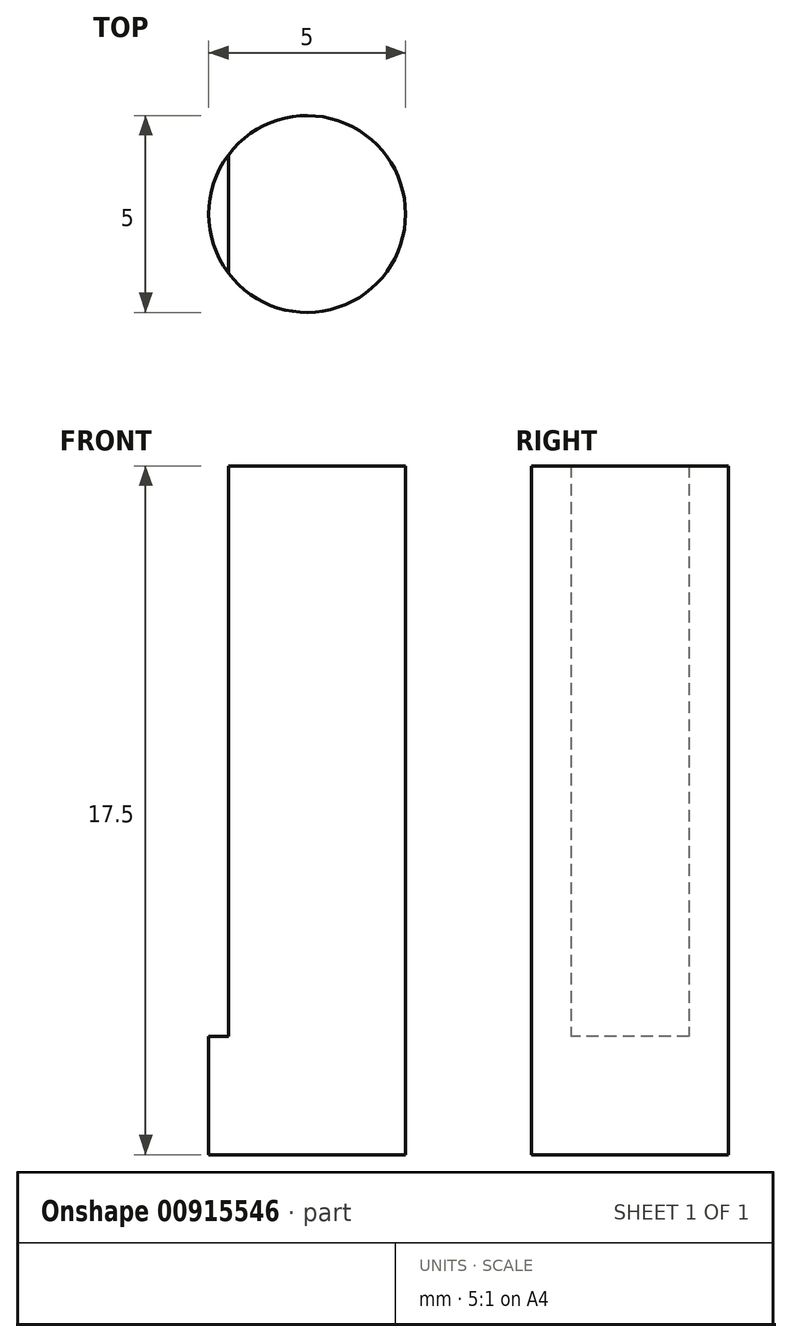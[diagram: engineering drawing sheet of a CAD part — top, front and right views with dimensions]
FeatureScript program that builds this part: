
annotation { "Feature Type Name" : "Feature", "Feature Type Description" : "" }
export const myFeature = defineFeature(function(context is Context, id is Id, definition is map)
    precondition{}
    {
        {
            var Q0;
            Q0=qCreatedBy(makeId("Top.planeOp"),FACE);
            var sketch = newSketch(context, id + "F0", { "sketchPlane" : qUnion([Q0])});
            skCircle(sketch, "E0.0", {"center": v(0, 0) * mm, "radius": 11 * mm});
            skCircle(sketch, "E1.0", {"center": v(0, 0) * mm, "radius": 16.5 * mm});
            skCircle(sketch, "E2.0", {"center": v(0, 0) * mm, "radius": 2.5 * mm});
            skLineSegment(sketch, "E3.0", {"start": v(-2, 1.5) * mm, "end": v(-2, -1.5) * mm});
            skSolve(sketch);
        }
        {
            var Q0;
            {var subQ0=sQuery(id+"F0.wireOp",EDGE,"E3.0");Q0=makeQuery(id+"F0.imprint","IMPRINT",FACE,{"disambiguationData":[TD([[makeQuery(id+"F0.imprint","IMPRINT",EDGE,{"derivedFrom":subQ0}),1.0]])]});}
            extrude(context, id + "F1", {"entities" : qUnion([Q0]), "depth" : 17.5 * mm, "offsetDistance" : 25 * mm});
        }
        {
            var Q0;
            {var subQ0=sQuery(id+"F0.wireOp",EDGE,"E3.0");Q0=makeQuery(id+"F0.imprint","IMPRINT",FACE,{"disambiguationData":[TD([[makeQuery(id+"F0.imprint","IMPRINT",EDGE,{"derivedFrom":subQ0}),-1.0]])]});}
            extrude(context, id + "F2", {"entities" : qUnion([Q0]), "operationType" : NewBodyOperationType.ADD, "depth" : 3 * mm, "offsetDistance" : 25 * mm});
        }
    });
